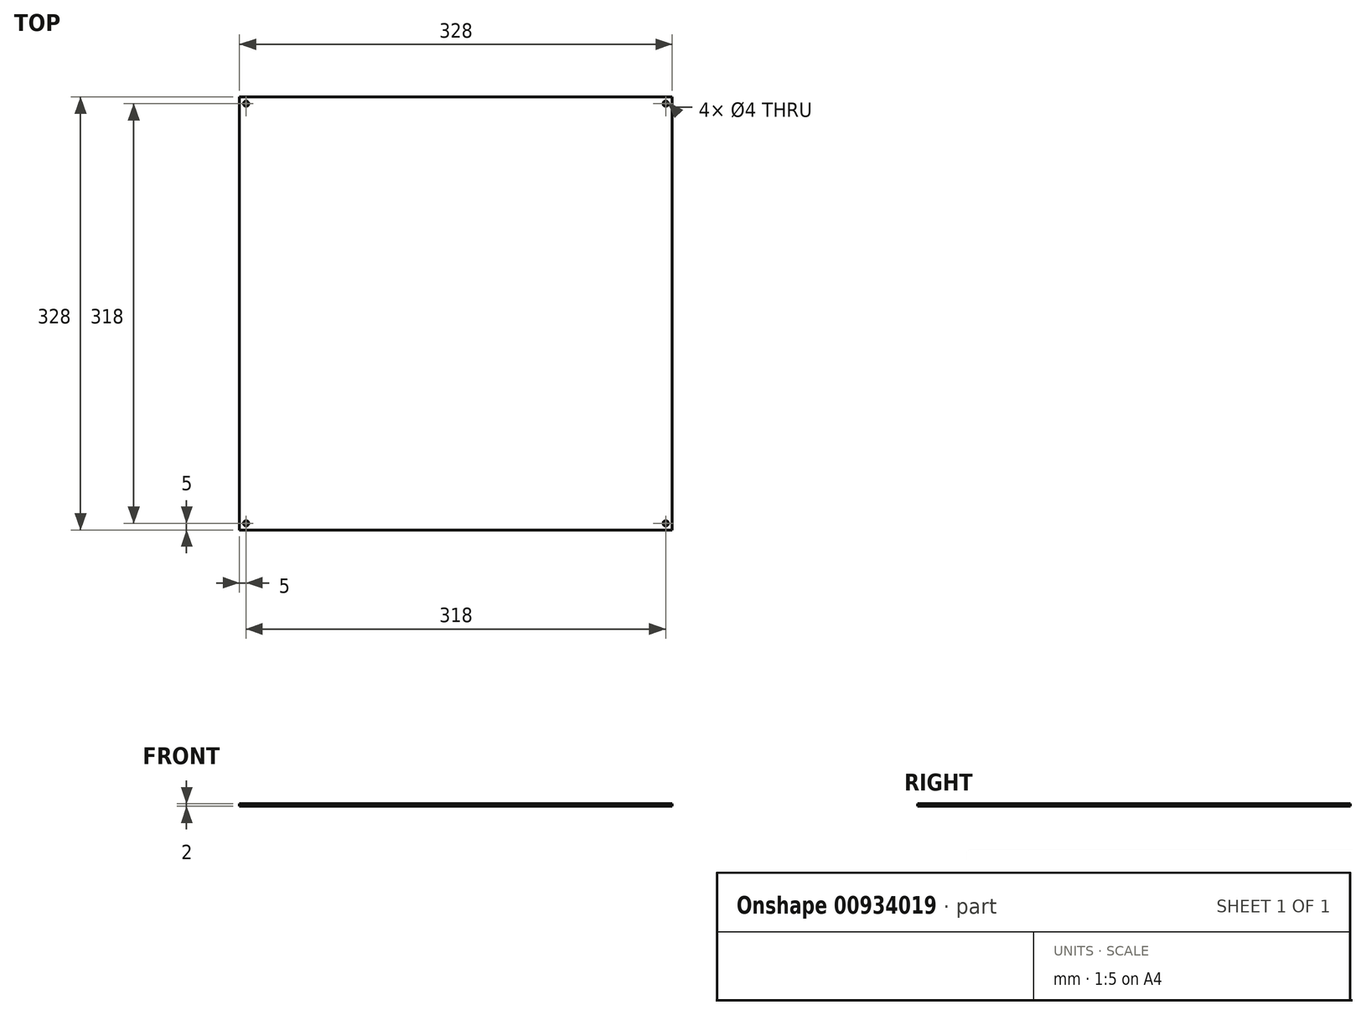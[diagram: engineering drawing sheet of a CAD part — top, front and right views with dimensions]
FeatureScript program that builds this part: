
annotation { "Feature Type Name" : "Feature", "Feature Type Description" : "" }
export const myFeature = defineFeature(function(context is Context, id is Id, definition is map)
    precondition{}
    {
        {
            var Q0;
            Q0=qCreatedBy(makeId("Top.planeOp"),FACE);
            var sketch = newSketch(context, id + "F0", { "sketchPlane" : qUnion([Q0])});
            skLineSegment(sketch, "E0.bottom", {"start": v(0, 0) * mm, "end": v(328, 0) * mm});
            skLineSegment(sketch, "E0.top", {"start": v(0, 328) * mm, "end": v(328, 328) * mm});
            skLineSegment(sketch, "E0.left", {"start": v(0, 0) * mm, "end": v(0, 328) * mm});
            skLineSegment(sketch, "E0.right", {"start": v(328, 0) * mm, "end": v(328, 328) * mm});
            skCircle(sketch, "E1", {"center": v(5, 5) * mm, "radius": 2 * mm});
            skLineSegment(sketch, "E2", {"start": v(164, 0) * mm, "end": v(164, 328) * mm, "construction": true});
            skLineSegment(sketch, "E3", {"start": v(0, 164) * mm, "end": v(328, 164) * mm, "construction": true});
            skCircle(sketch, "E4.MirrorC", {"center": v(323, 5) * mm, "radius": 2 * mm});
            skCircle(sketch, "E5.MirrorC", {"center": v(323, 323) * mm, "radius": 2 * mm});
            skCircle(sketch, "E6.MirrorC", {"center": v(5, 323) * mm, "radius": 2 * mm});
            skSolve(sketch);
        }
        {
            var Q0;
            Q0=qSketchRegion(id+"F0",true);
            extrude(context, id + "F1", {"entities" : qUnion([Q0]), "depth" : 2 * mm, "offsetDistance" : 25 * mm});
        }
    });
